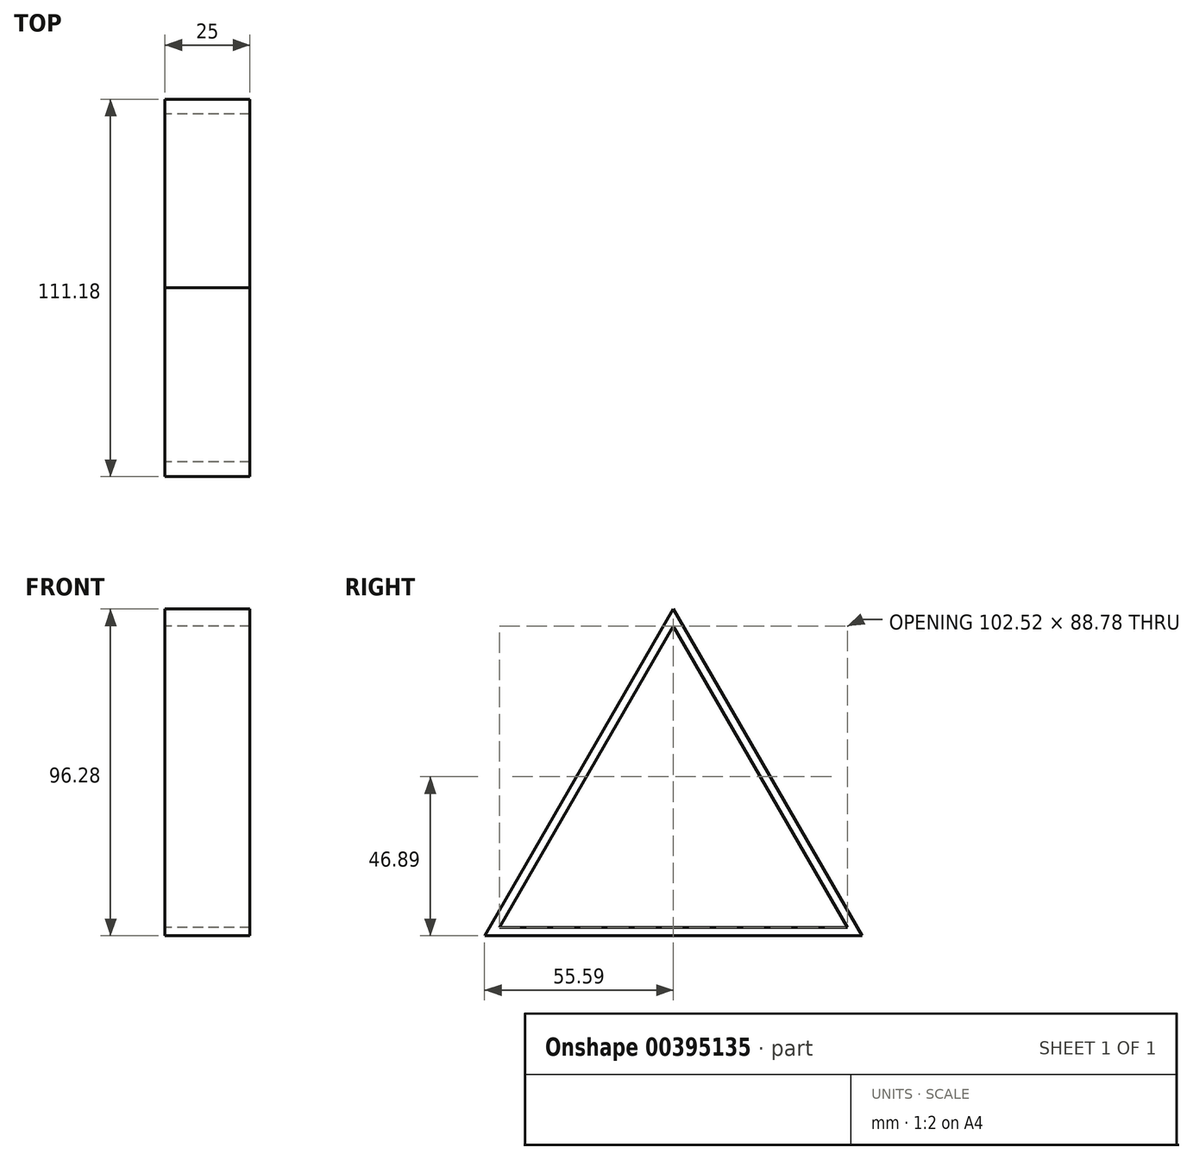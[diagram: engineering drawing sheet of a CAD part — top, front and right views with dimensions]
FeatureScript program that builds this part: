
annotation { "Feature Type Name" : "Feature", "Feature Type Description" : "" }
export const myFeature = defineFeature(function(context is Context, id is Id, definition is map)
    precondition{}
    {
        {
            var Q0;
            Q0=qCreatedBy(makeId("Right.planeOp"),FACE);
            var sketch = newSketch(context, id + "F0", { "sketchPlane" : qUnion([Q0])});
            skLineSegment(sketch, "E0", {"start": v(0, 51.4) * mm, "end": v(-55.59, -44.88) * mm});
            skLineSegment(sketch, "E1", {"start": v(-55.59, -44.88) * mm, "end": v(55.59, -44.88) * mm});
            skLineSegment(sketch, "E2", {"start": v(55.59, -44.88) * mm, "end": v(0, 51.4) * mm});
            skSolve(sketch);
        }
        {
            var Q0;
            Q0=makeQuery(id+"F0.imprint","IMPRINT",FACE,{"disambiguationData":[TD([[makeQuery(id+"F0.imprint","IMPRINT",EDGE,{"derivedFrom":sQuery(id+"F0.wireOp",EDGE,"E0")}),1.0]])]});
            var sketch = newSketch(context, id + "F1", { "sketchPlane" : qUnion([Q0])});
            skLineSegment(sketch, "E3.0", {"start": v(-51.26, -42.38) * mm, "end": v(51.26, -42.38) * mm});
            skLineSegment(sketch, "E3.1", {"start": v(0, 46.4) * mm, "end": v(-51.26, -42.38) * mm});
            skLineSegment(sketch, "E3.2", {"start": v(51.26, -42.38) * mm, "end": v(0, 46.4) * mm});
            skSolve(sketch);
        }
        {
            var Q0;
            Q0=makeQuery(id+"F1.imprint","IMPRINT",FACE,{"disambiguationData":[TD([[makeQuery(id+"F1.imprint","IMPRINT",EDGE,{"derivedFrom":sQuery(id+"F1.wireOp",EDGE,"E3.0")}),-1.0]])]});
            extrude(context, id + "F2", {"entities" : qUnion([Q0]), "depth" : 25 * mm});
        }
    });
